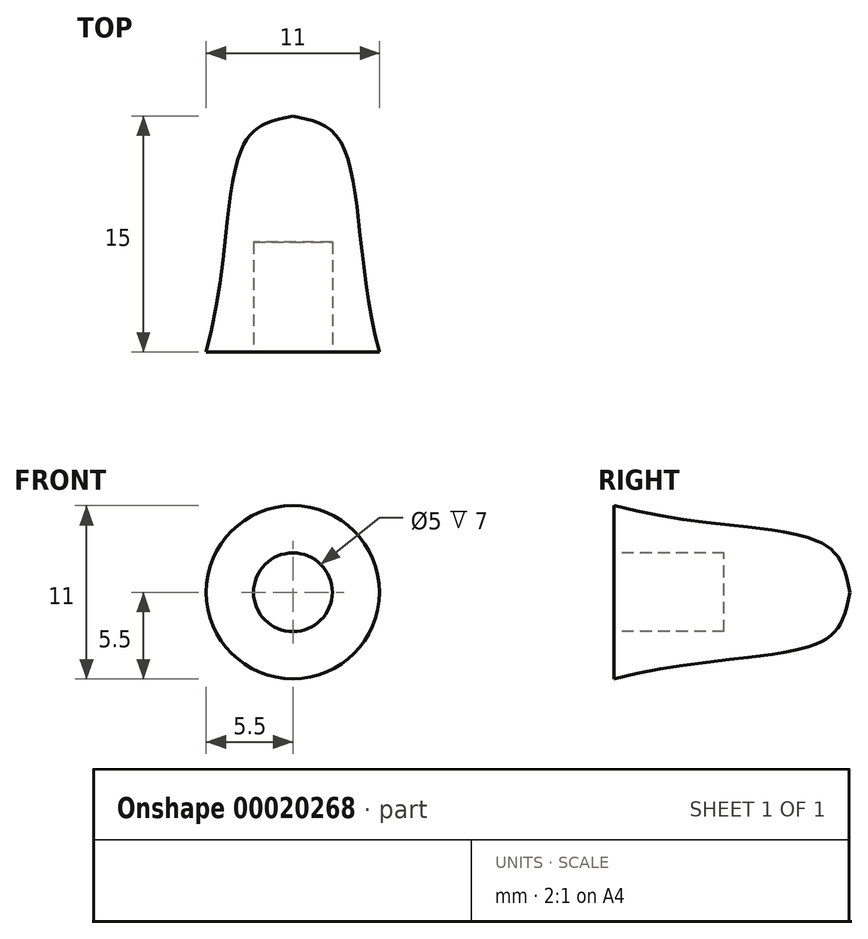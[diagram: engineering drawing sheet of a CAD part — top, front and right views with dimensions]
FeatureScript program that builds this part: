
annotation { "Feature Type Name" : "Feature", "Feature Type Description" : "" }
export const myFeature = defineFeature(function(context is Context, id is Id, definition is map)
    precondition{}
    {
        {
            var Q0;
            Q0=qCreatedBy(makeId("Top.planeOp"),FACE);
            var sketch = newSketch(context, id + "F0", { "sketchPlane" : qUnion([Q0])});
            skLineSegment(sketch, "E0.bottom", {"start": v(2.5, 0) * mm, "end": v(5.5, 0) * mm});
            skLineSegment(sketch, "E0.left", {"start": v(0, 7) * mm, "end": v(0, 15) * mm});
            skFitSpline(sketch, "E1", {"points": [v(0, 15) * mm, v(2.9, 13.57) * mm, v(5.5, 0) * mm], "startDerivative": vector(9.3, -1.95) * mm, "endDerivative": vector(6.75, -25.27) * mm});
            skLineSegment(sketch, "E2.top", {"start": v(0, 7) * mm, "end": v(2.5, 7) * mm});
            skLineSegment(sketch, "E2.right", {"start": v(2.5, 0) * mm, "end": v(2.5, 7) * mm});
            skPoint(sketch, "E0.right.end.orphan", {"position": v(5.5, 15) * mm});
            skPoint(sketch, "E2.left.start.orphan", {"position": v(0, 0) * mm});
            skSolve(sketch);
        }
        {
            var Q0;
            Q0 = qSketchRegion(id + "F0", true);
            var Q1;
            Q1=sQuery(id+"F0.wireOp",EDGE,"E0.left");
            revolve(context, id + "F1", {"entities" : qUnion([Q0]), "axis" : qUnion([Q1]), "revolveType" : RevolveType.FULL});
        }
    });
